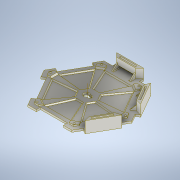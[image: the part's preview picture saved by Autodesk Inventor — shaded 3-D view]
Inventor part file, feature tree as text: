
AUTODESK INVENTOR PART (.ipt)
format: ipt  version: 2020 (Build 240168000, 168)  size: 553,984 bytes
history: native  units: mm
features: chamfer x9, extrude x8, sketch x2, pattern_circular x2, fillet x1
ambient origin geometry x8: Origin, YZ Plane, XZ Plane, XY Plane, X Axis, Y Axis, Z Axis, Center Point
bodies: Body1 (feature_tree)
feature tree (22):
  sketch  "Sketch6"  dims[d72=6.5mm d87=15.0mm]
  extrude  "Plate"  Depth=15.0mm
  extrude  "Cazzetti"  Depth=2.5mm
  extrude  "ScavoStrip"  Depth=2.5mm
  extrude  "ScalinoAllineamento"  Depth=2.5mm
  extrude  "Foro"  Depth=2.5mm
  extrude  "ForoMuro"  TaperAngle=0.0deg  [1 undecoded]
  extrude  "Scavi"  Depth=2.5mm
  chamfer  "Smussi"  Distance=3.0mm
  pattern_circular  "ScalinoCircolare"  [2 undecoded]
  chamfer  "Chamfer3"  Distance=15.0mm
  chamfer  "Chamfer4"  Distance=2.0mm
  chamfer  "Chamfer5"  Distance=13.0mm
  chamfer  "Chamfer6"  Distance=2.5mm
  chamfer  "Chamfer7"  Distance=26.0mm
  chamfer  "Chamfer8"  Distance=70.0mm
  extrude  "Nervature"  Depth=2.5mm
  chamfer  "SmussoNervature"  Distance=1.25mm
  pattern_circular  "Circular Pattern2"  [2 undecoded]
  fillet  "Raccordo"  Radius=5.0mm
  chamfer  "ForoSmusso"  Distance=2.0mm
  sketch  "Sketch10"  dims[d88=6.5mm d92=2.5mm d95=1.25mm d96=25.0mm d98=25.0mm d100=0.0mm d105=30.0mm d106=3.0mm d107=0.0mm d108=6.5mm d112=15.0mm d113=2.0mm d114=13.0mm d115=2.5mm d116=26.0mm d118=70.0mm d119=54.121778mm d120=1.25mm d121=15.0mm d122=0.0mm d125=5.0mm d126=0.0mm d127=2.0mm d130=7.0mm d131=2.0mm d132=0.0mm d133=60.0mm d134=360.0deg d136=4.0mm d138=3.0mm d139=3.0mm d140=9.25mm d141=0.0mm d142=20.0mm d143=30.0mm d145=3.5mm d146=4.0mm d147=10.0mm d148=0.0mm d149=7.0mm d150=2.5mm d152=6.4mm d154=6.4mm d155=30.0mm d157=120.0deg d159=60.0mm d161=360.0deg d163=2.0mm d164=2.0mm d165=45.0deg d166=1.5mm d167=0.0mm d171=1.5mm d172=2.0mm d173=45.0deg d174=1.5mm d175=2.0mm d176=45.0deg d177=1.5mm d178=2.0mm d179=45.0deg d180=1.5mm d181=2.0mm d182=45.0deg d183=1.5mm d184=2.0mm d185=45.0deg d186=1.5mm d187=2.0mm d188=45.0deg d189=2.0mm d190=8.0mm d191=8.0mm d192=0.0mm d193=8.0mm d194=2.0mm d195=45.0deg d196=30.0mm d197=120.0deg d199=1.0mm d200=1.0mm d201=2.0mm d202=45.0deg d205=6.6mm d128=0.872665mm d160=0.872665mm d162=0.872665mm]
note: 5 required parameter values undecoded (feature->parameter linkage not recoverable at this tier; creation-order binding heuristic only, values carry confidence <= 0.55)
